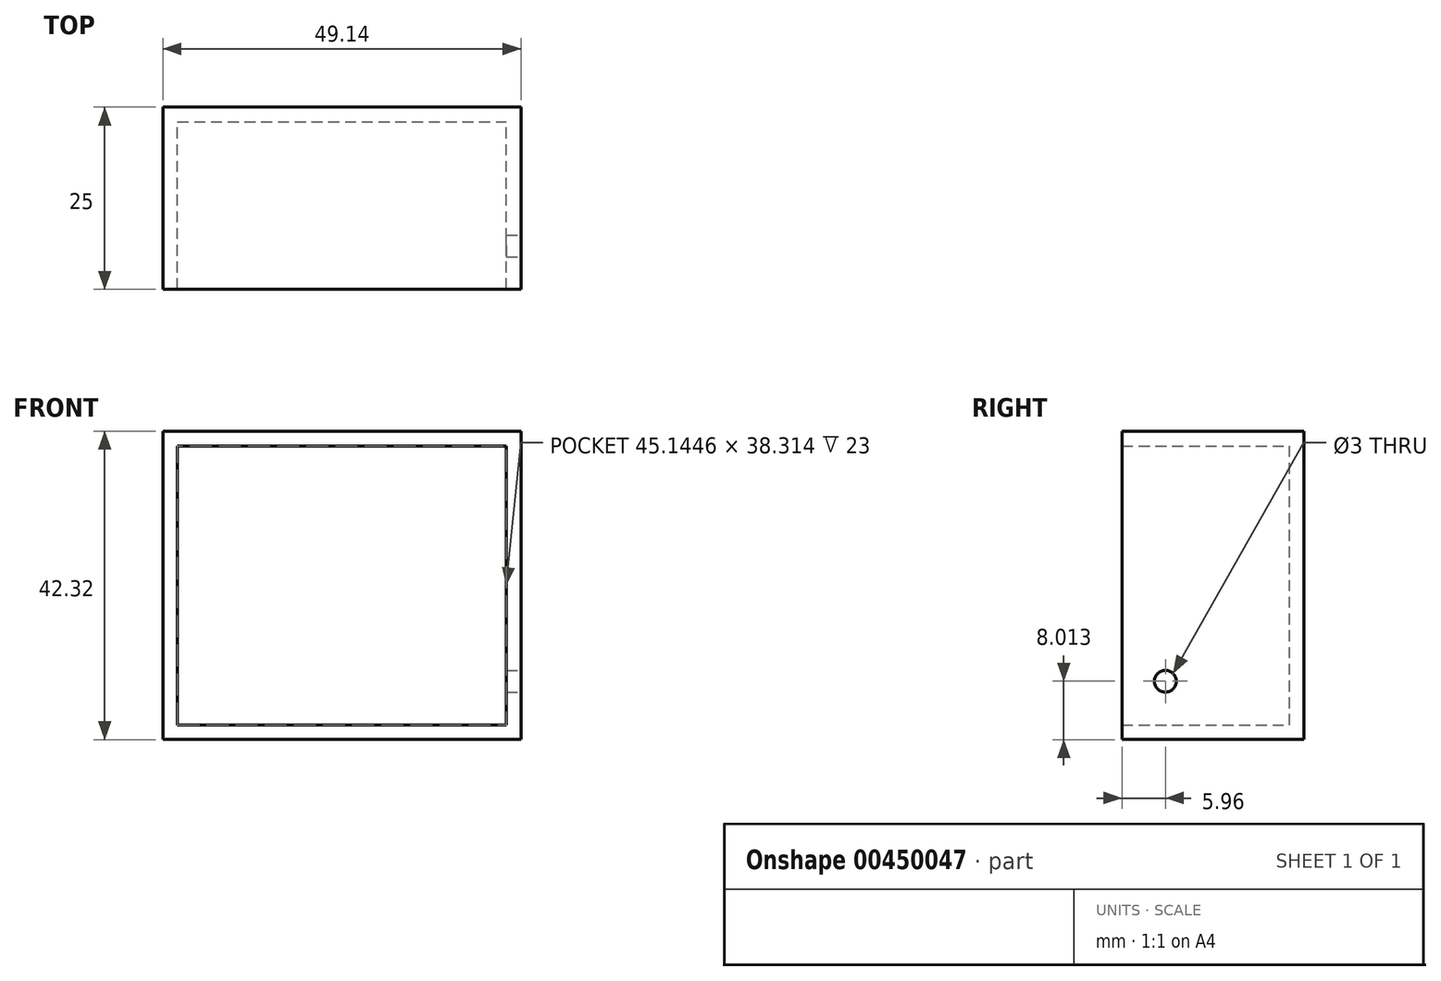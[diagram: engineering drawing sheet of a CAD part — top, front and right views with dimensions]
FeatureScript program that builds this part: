
annotation { "Feature Type Name" : "Feature", "Feature Type Description" : "" }
export const myFeature = defineFeature(function(context is Context, id is Id, definition is map)
    precondition{}
    {
        {
            var Q0;
            Q0=qCreatedBy(makeId("Front.planeOp"),FACE);
            var sketch = newSketch(context, id + "F0", { "sketchPlane" : qUnion([Q0])});
            skLineSegment(sketch, "E0.bottom", {"start": v(-23.91, -21.16) * mm, "end": v(25.23, -21.16) * mm});
            skLineSegment(sketch, "E0.top", {"start": v(-23.91, 21.16) * mm, "end": v(25.23, 21.16) * mm});
            skLineSegment(sketch, "E0.left", {"start": v(-23.91, -21.16) * mm, "end": v(-23.91, 21.16) * mm});
            skLineSegment(sketch, "E0.right", {"start": v(25.23, -21.16) * mm, "end": v(25.23, 21.16) * mm});
            skPoint(sketch, "E0.middle", {"position": v(0.66, 0) * mm});
            skLineSegment(sketch, "E1.0", {"start": v(-21.91, -19.16) * mm, "end": v(-21.91, 19.16) * mm});
            skLineSegment(sketch, "E1.1", {"start": v(-21.91, -19.16) * mm, "end": v(23.23, -19.16) * mm});
            skLineSegment(sketch, "E1.2", {"start": v(23.23, -19.16) * mm, "end": v(23.23, 19.16) * mm});
            skLineSegment(sketch, "E1.3", {"start": v(-21.91, 19.16) * mm, "end": v(23.23, 19.16) * mm});
            skSolve(sketch);
        }
        {
            var Q0;
            Q0=makeQuery(id+"F0.imprint","IMPRINT",FACE,{"disambiguationData":[TD([[makeQuery(id+"F0.imprint","IMPRINT",EDGE,{"derivedFrom":sQuery(id+"F0.wireOp",EDGE,"E1.0")}),-1.0]])]});
            extrude(context, id + "F1", {"entities" : qUnion([Q0]), "depth" : 2 * mm});
        }
        {
            var Q0;
            Q0 = qSketchRegion(id + "F0", true);
            extrude(context, id + "F2", {"entities" : qUnion([Q0]), "operationType" : NewBodyOperationType.ADD, "depth" : 25 * mm});
        }
        {
            var Q0;
            Q0=makeQuery(id+"F2.opExtrude","SWEPT_FACE",FACE,{"disambiguationData":[OSD([sQuery(id+"F0.wireOp",EDGE,"E0.right")])]});
            var sketch = newSketch(context, id + "F3", { "sketchPlane" : qUnion([Q0])});
            skCircle(sketch, "E2", {"center": v(-19.04, -13.15) * mm, "radius": 1.5 * mm});
            skSolve(sketch);
        }
        {
            var Q0;
            Q0=makeQuery(id+"F3.imprint","IMPRINT",FACE,{"disambiguationData":[TD([[makeQuery(id+"F3.imprint","IMPRINT",EDGE,{"derivedFrom":sQuery(id+"F3.wireOp",EDGE,"E2")}),1.0]])]});
            extrude(context, id + "F4", {"entities" : qUnion([Q0]), "operationType" : NewBodyOperationType.REMOVE, "endBound" : BoundingType.UP_TO_NEXT, "oppositeDirection" : true, "depth" : 25 * mm});
        }
    });
